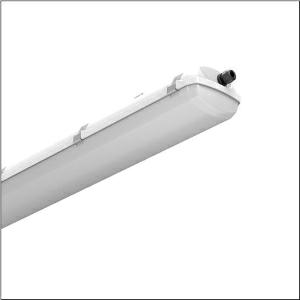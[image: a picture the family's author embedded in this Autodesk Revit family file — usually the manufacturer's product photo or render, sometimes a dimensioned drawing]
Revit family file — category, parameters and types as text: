
# Revit family: monsun_r__ex_51fxa27l860a_0ded
name_source: partatom
category: Lighting Fixtures
units: mm (PartAtom-declared; Revit-internal decimal feet)

## family parameters
Cut with Voids When Loaded = No
Host = Face
Light Source = No
Part Type = Normal
Room Calculation Point = No
Round Connector Dimension = Use Diameter
Shared = No

## types (1)
- Monsun® Ex (1 x LED, 6560 lm, 53 W, 6500K)
    Apparent Load = 53 VA
    CIE Flux Codes = 46 76 94 98 100
    Color Rendering = 80
    Color Temperature = 6500K
    Default Elevation = 1800 mm
    Description = Monsun® Ex, damp-proof luminaire, primary optical cover: cover, of PC, UV-stabilised, opal, light emission: direct distribution, primary light characteristic: symmetric, installation type: surface-mounted, LED, rated luminous flux: 6.560lm, luminous efficacy: 124lm/W, light colour: 860, colour temperature: 6000K, control gear: ECG, with terminal, 3-pole, max. 2.5mm², through-wiring: 5x 2.5mm², mains connection: 220..250V, AC, 50/60Hz, rated input power: 53W, housing, of PC, light grey (RAL 7035), incl. 1x Ex cable gland M20 for cable diameter 7..12mm with sealing, incl. 1x Ex locking screw M20 with sealing, length: 1.280mm, width: 155mm, height: 105mm, clip for enclosure, of stainless steel, protection rating (complete): IP66, insulation class (complete): insulation class I (protective earthing), certification: CE, explosion class: zone 1,21 II 2G Ex eb mb op is IIC T4 Gb, II 2D Ex tb op is IIIC T67°C Db, impact resistance: IK10, permissible operating ambient temperature: -20..+40°C, contact your sales advisor before using the luminaires in applications with unclear chemical exposure, large temperature fluctuations or condensation-forming humidity, packaging unit: 1 piece
    Height = 105 mm
    Lamp = 1 x LED
    Lamp Light Flux = 6560 lm
    Lamp Power = 53 W
    Lamp count = 1
    Length = 1280 mm
    Luminous efficacy = 124 lm/W
    Manufacturer = Siteco
    ModVariant = No
    Model = 51FXA27L860A
    Mounting Place = Ceiling
    Mounting Type = Surface mounted
    Number of Poles = 1
    OnlyDefault = Yes
    Power Factor = 1
    Product Name = Monsun® Ex
    Product group = damp-proof luminaire
    ProductGroupID = 300
    Protection Class = Protection class I
    Protection Degree = IP 66
    RLX_Detail_Level = 1
    RLX_Emergency_Light_Flux = 0 lm
    RLX_Emergency_Type = 0
    RLX_Emergency_Type_DB = No
    RlxData = <blob elided: 41629 chars, md5=bb981950>
    Socket = socket
    Standby Power = 0 W
    System Light Flux = 6560 lm
    System Power = 53 W
    Type Comments = Product without accessories
    Type Image = l_1258882.jpg
    URL = http://relux.com
    VarID = ---
    Voltage = 0 V
    Weight = 0.00 kg
    Width = 155 mm

## geometry (parser evidence)
native form markers: Blend x4, Sweep x11
no freeform markers — native parametric forms only
